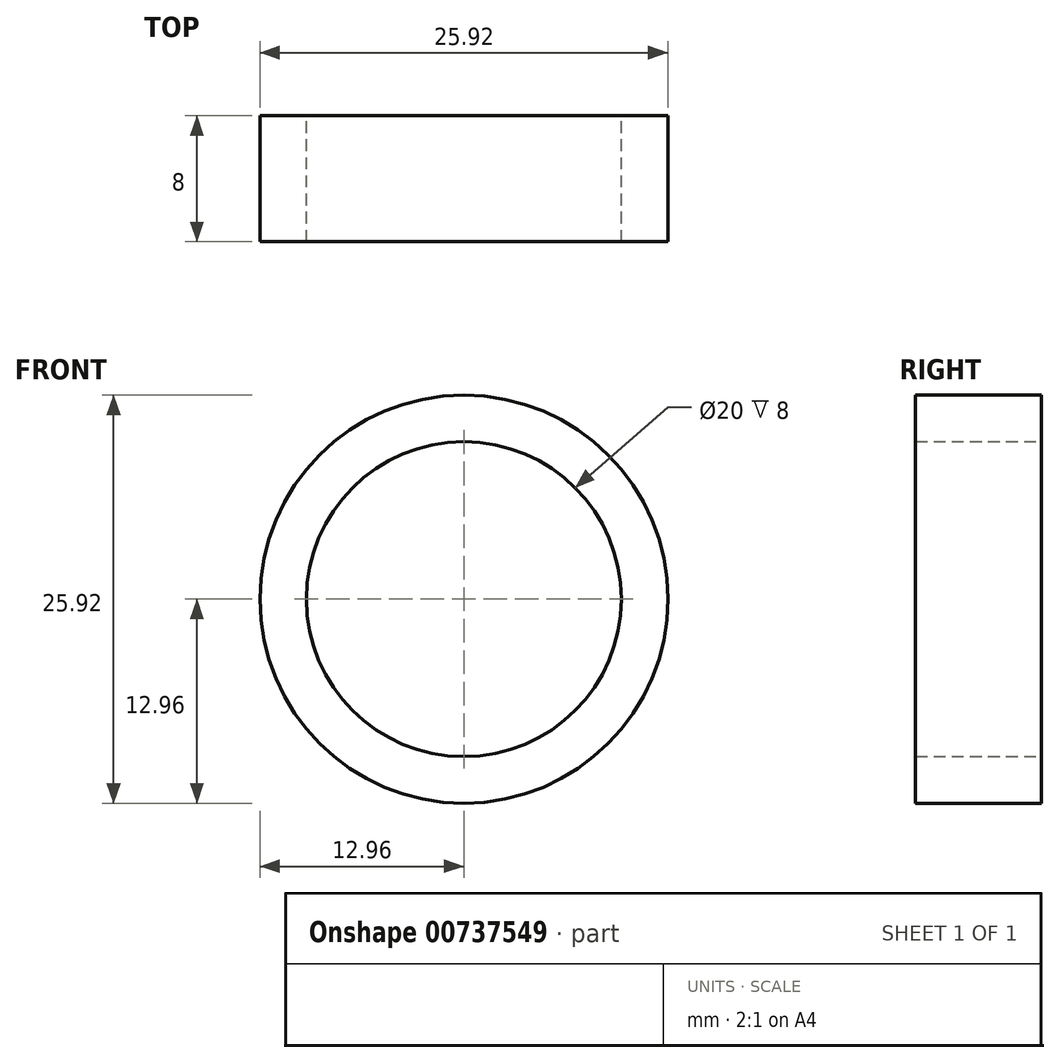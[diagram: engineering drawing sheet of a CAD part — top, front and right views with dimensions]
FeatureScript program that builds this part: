
annotation { "Feature Type Name" : "Feature", "Feature Type Description" : "" }
export const myFeature = defineFeature(function(context is Context, id is Id, definition is map)
    precondition{}
    {
        {
            var Q0;
            Q0=qCreatedBy(makeId("Front.planeOp"),FACE);
            var sketch = newSketch(context, id + "F0", { "sketchPlane" : qUnion([Q0])});
            skCircle(sketch, "E0", {"center": v(0, 0) * mm, "radius": 12.96 * mm});
            skCircle(sketch, "E1", {"center": v(0, 0) * mm, "radius": 10 * mm});
            skSolve(sketch);
        }
        {
            var Q0;
            Q0 = qSketchRegion(id + "F0", true);
            extrude(context, id + "F1", {"entities" : qUnion([Q0]), "depth" : 8 * mm, "offsetDistance" : 25 * mm});
        }
    });
